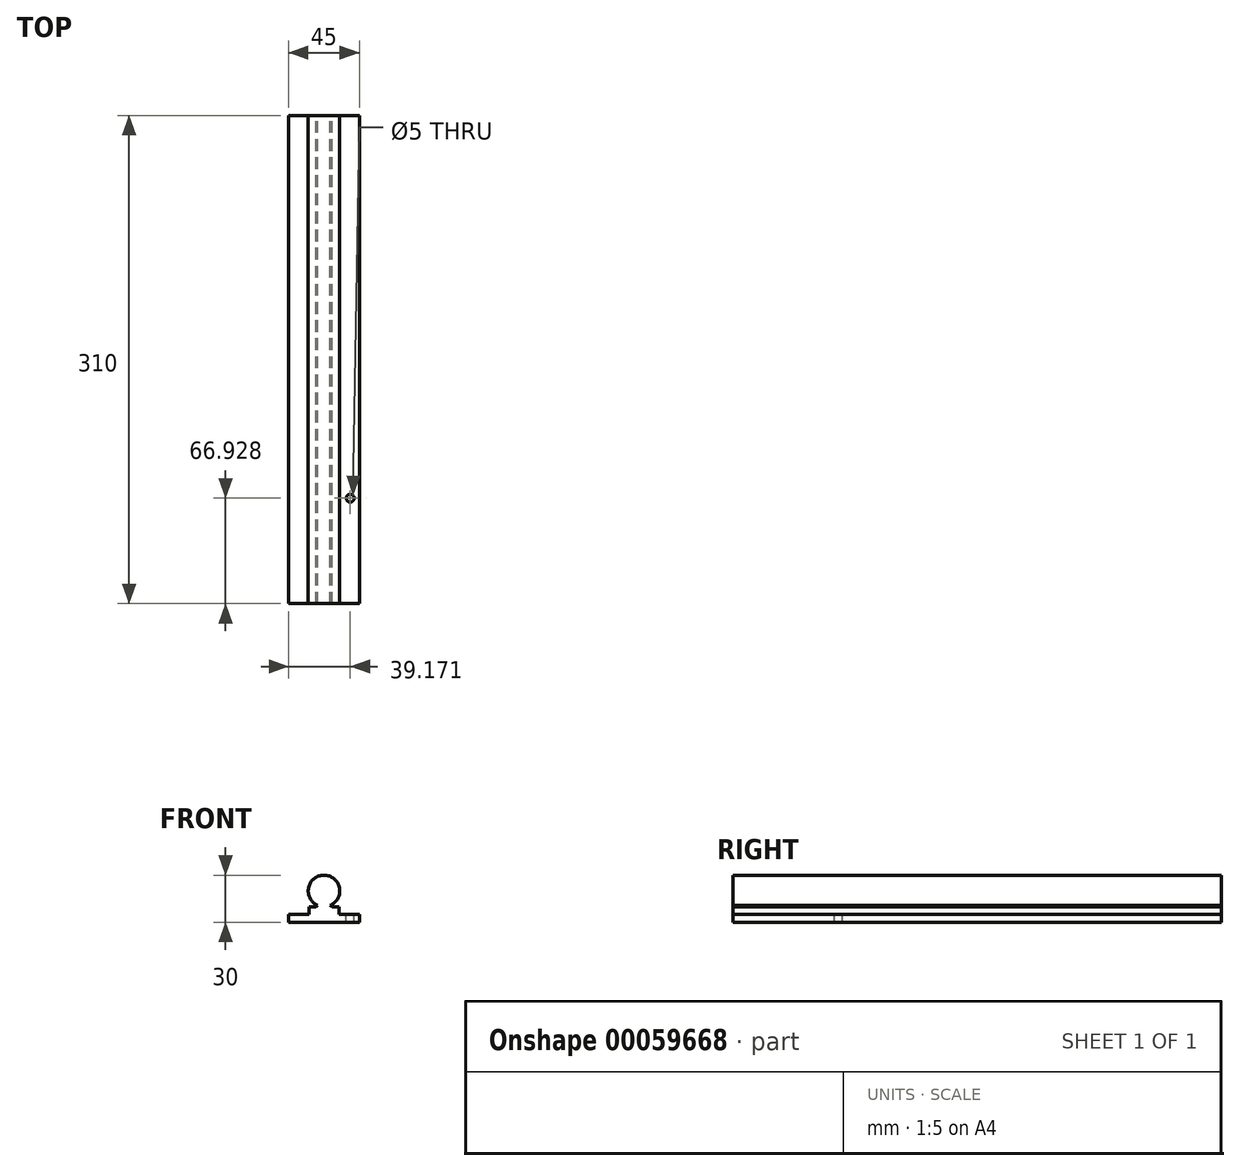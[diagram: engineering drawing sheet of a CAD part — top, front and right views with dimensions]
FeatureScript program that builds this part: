
annotation { "Feature Type Name" : "Feature", "Feature Type Description" : "" }
export const myFeature = defineFeature(function(context is Context, id is Id, definition is map)
    precondition{}
    {
        {
            var Q0;
            Q0=qCreatedBy(makeId("Front.planeOp"),FACE);
            var sketch = newSketch(context, id + "F0", { "sketchPlane" : qUnion([Q0])});
            skLineSegment(sketch, "E0", {"start": v(0, 0) * mm, "end": v(22.5, 0) * mm});
            skLineSegment(sketch, "E1", {"start": v(22.5, 0) * mm, "end": v(22.5, 5) * mm});
            skLineSegment(sketch, "E2", {"start": v(22.5, 5) * mm, "end": v(9.5, 5) * mm});
            skLineSegment(sketch, "E3", {"start": v(9.5, 5) * mm, "end": v(9.5, 10) * mm});
            skLineSegment(sketch, "E4", {"start": v(9.5, 10) * mm, "end": v(5, 10) * mm});
            skLineSegment(sketch, "E5", {"start": v(5, 10) * mm, "end": v(4, 10.83) * mm});
            skArc(sketch, "E6", {"start": v(0, 10) * mm, "mid": v(10, 20) * mm, "end": v(0, 30) * mm});
            skLineSegment(sketch, "E7", {"start": v(0, 0) * mm, "end": v(0, 31.1) * mm, "construction": true});
            skArc(sketch, "E8.MirrorCS", {"start": v(0, 10) * mm, "mid": v(-10, 20) * mm, "end": v(0, 30) * mm});
            skLineSegment(sketch, "E9.MirrorCS", {"start": v(-5, 10) * mm, "end": v(-4, 10.83) * mm});
            skLineSegment(sketch, "E10.MirrorCS", {"start": v(-9.5, 10) * mm, "end": v(-5, 10) * mm});
            skLineSegment(sketch, "E11.MirrorCS", {"start": v(-9.5, 5) * mm, "end": v(-9.5, 10) * mm});
            skLineSegment(sketch, "E12.MirrorCS", {"start": v(-22.5, 5) * mm, "end": v(-9.5, 5) * mm});
            skLineSegment(sketch, "E13.MirrorCS", {"start": v(0, 0) * mm, "end": v(-22.5, 0) * mm});
            skLineSegment(sketch, "E14.MirrorCS", {"start": v(-22.5, 0) * mm, "end": v(-22.5, 5) * mm});
            skSolve(sketch);
        }
        {
            var Q0;
            {var subQ0=sQuery(id+"F0.wireOp",EDGE,"E6");var subQ1=makeQuery(id+"F0.imprint","INTERSECT",VERTEX,{"derivedFrom":[sQuery(id+"F0.wireOp",EDGE,"E5"),subQ0]});Q0=makeQuery(id+"F0.imprint","IMPRINT",FACE,{"disambiguationData":[TD([[makeQuery(id+"F0.imprint","IMPRINT",EDGE,{"disambiguationData":[TD([[subQ1,1.0]])],"derivedFrom":subQ0}),1.0]])]});}
            var Q1;
            Q1=makeQuery(id+"F0.imprint","IMPRINT",FACE,{"disambiguationData":[TD([[makeQuery(id+"F0.imprint","IMPRINT",EDGE,{"derivedFrom":sQuery(id+"F0.wireOp",EDGE,"E0")}),1.0]])]});
            extrude(context, id + "F1", {"entities" : qUnion([Q0, Q1]), "depth" : 310 * mm});
        }
        {
            var Q0;
            Q0=makeQuery(id+"F1.opExtrude","SWEPT_FACE",FACE,{"disambiguationData":[OSD([sQuery(id+"F0.wireOp",EDGE,"E2")])]});
            var sketch = newSketch(context, id + "F2", { "sketchPlane" : qUnion([Q0])});
            skPoint(sketch, "E15", {"position": v(16.67, -243.07) * mm});
            skSolve(sketch);
        }
        {
            var Q0;
            Q0=sQuery(id+"F2.wireOp",VERTEX,"E15");
            var Q1;
            Q1=makeQuery(id+"F1.opExtrude","SWEPT_BODY",BODY,{"disambiguationData":[OSD([sQuery(id+"F0.wireOp",EDGE,"E0"),sQuery(id+"F0.wireOp",EDGE,"E1"),sQuery(id+"F0.wireOp",EDGE,"E2"),sQuery(id+"F0.wireOp",EDGE,"E3"),sQuery(id+"F0.wireOp",EDGE,"E4"),sQuery(id+"F0.wireOp",EDGE,"E5"),sQuery(id+"F0.wireOp",EDGE,"E6"),sQuery(id+"F0.wireOp",EDGE,"E8.MirrorCS"),sQuery(id+"F0.wireOp",EDGE,"E9.MirrorCS"),sQuery(id+"F0.wireOp",EDGE,"E10.MirrorCS"),sQuery(id+"F0.wireOp",EDGE,"E11.MirrorCS"),sQuery(id+"F0.wireOp",EDGE,"E12.MirrorCS"),sQuery(id+"F0.wireOp",EDGE,"E13.MirrorCS"),sQuery(id+"F0.wireOp",EDGE,"E14.MirrorCS")])]});
            hole(context, id + "F3", {"style" : HoleStyle.SIMPLE, "holeDiameter" : 5 * mm, "endStyle" : HoleEndStyle.THROUGH, "locations" : qUnion([Q0]), "scope" : qUnion([Q1])});
        }
    });
